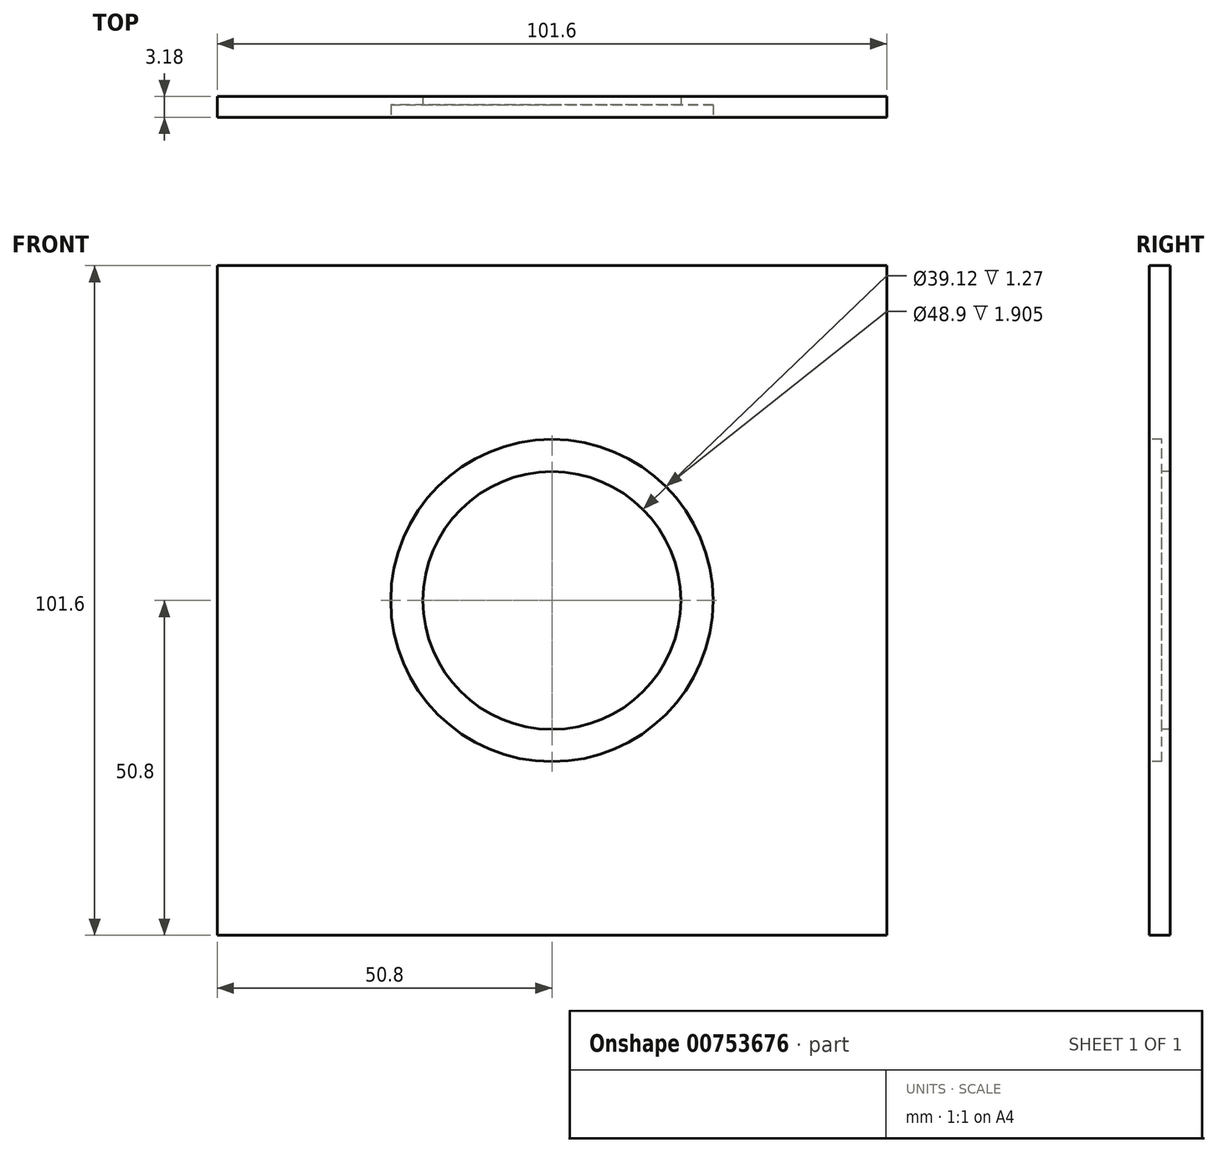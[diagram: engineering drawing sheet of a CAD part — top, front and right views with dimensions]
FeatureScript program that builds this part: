
annotation { "Feature Type Name" : "Feature", "Feature Type Description" : "" }
export const myFeature = defineFeature(function(context is Context, id is Id, definition is map)
    precondition{}
    {
        {
            var Q0;
            Q0=qCreatedBy(makeId("Front.planeOp"),FACE);
            var sketch = newSketch(context, id + "F0", { "sketchPlane" : qUnion([Q0])});
            skLineSegment(sketch, "E0.bottom", {"start": v(50.8, 50.8) * mm, "end": v(-50.8, 50.8) * mm});
            skLineSegment(sketch, "E0.top", {"start": v(50.8, -50.8) * mm, "end": v(-50.8, -50.8) * mm});
            skLineSegment(sketch, "E0.left", {"start": v(50.8, 50.8) * mm, "end": v(50.8, -50.8) * mm});
            skLineSegment(sketch, "E0.right", {"start": v(-50.8, 50.8) * mm, "end": v(-50.8, -50.8) * mm});
            skPoint(sketch, "E0.middle", {"position": v(0, 0) * mm});
            skSolve(sketch);
        }
        {
            var Q0;
            Q0 = qSketchRegion(id + "F0", true);
            extrude(context, id + "F1", {"entities" : qUnion([Q0]), "depth" : 3.17 * mm, "offsetDistance" : 25.4 * mm});
        }
        {
            var Q0;
            Q0=makeQuery(id+"F1.opExtrude","CAP_FACE",FACE,{"disambiguationData":[OSD([sQuery(id+"F0.wireOp",EDGE,"E0.bottom"),sQuery(id+"F0.wireOp",EDGE,"E0.top"),sQuery(id+"F0.wireOp",EDGE,"E0.left"),sQuery(id+"F0.wireOp",EDGE,"E0.right")])],"isStart":false});
            var sketch = newSketch(context, id + "F2", { "sketchPlane" : qUnion([Q0])});
            skCircle(sketch, "E1", {"center": v(0, 0) * mm, "radius": 19.56 * mm});
            skSolve(sketch);
        }
        {
            var Q0;
            Q0 = qSketchRegion(id + "F2", true);
            extrude(context, id + "F3", {"entities" : qUnion([Q0]), "operationType" : NewBodyOperationType.REMOVE, "endBound" : BoundingType.THROUGH_ALL, "oppositeDirection" : true, "depth" : 25.4 * mm, "offsetDistance" : 25.4 * mm});
        }
        {
            var Q0;
            Q0=makeQuery(id+"F1.opExtrude","CAP_FACE",FACE,{"disambiguationData":[OSD([sQuery(id+"F0.wireOp",EDGE,"E0.bottom"),sQuery(id+"F0.wireOp",EDGE,"E0.top"),sQuery(id+"F0.wireOp",EDGE,"E0.left"),sQuery(id+"F0.wireOp",EDGE,"E0.right")])],"isStart":false});
            var sketch = newSketch(context, id + "F4", { "sketchPlane" : qUnion([Q0])});
            skCircle(sketch, "E2", {"center": v(0, 0) * mm, "radius": 24.45 * mm});
            skSolve(sketch);
        }
        {
            var Q0;
            Q0 = qSketchRegion(id + "F4", true);
            extrude(context, id + "F5", {"entities" : qUnion([Q0]), "operationType" : NewBodyOperationType.REMOVE, "oppositeDirection" : true, "depth" : 1.9 * mm, "offsetDistance" : 25.4 * mm});
        }
    });
